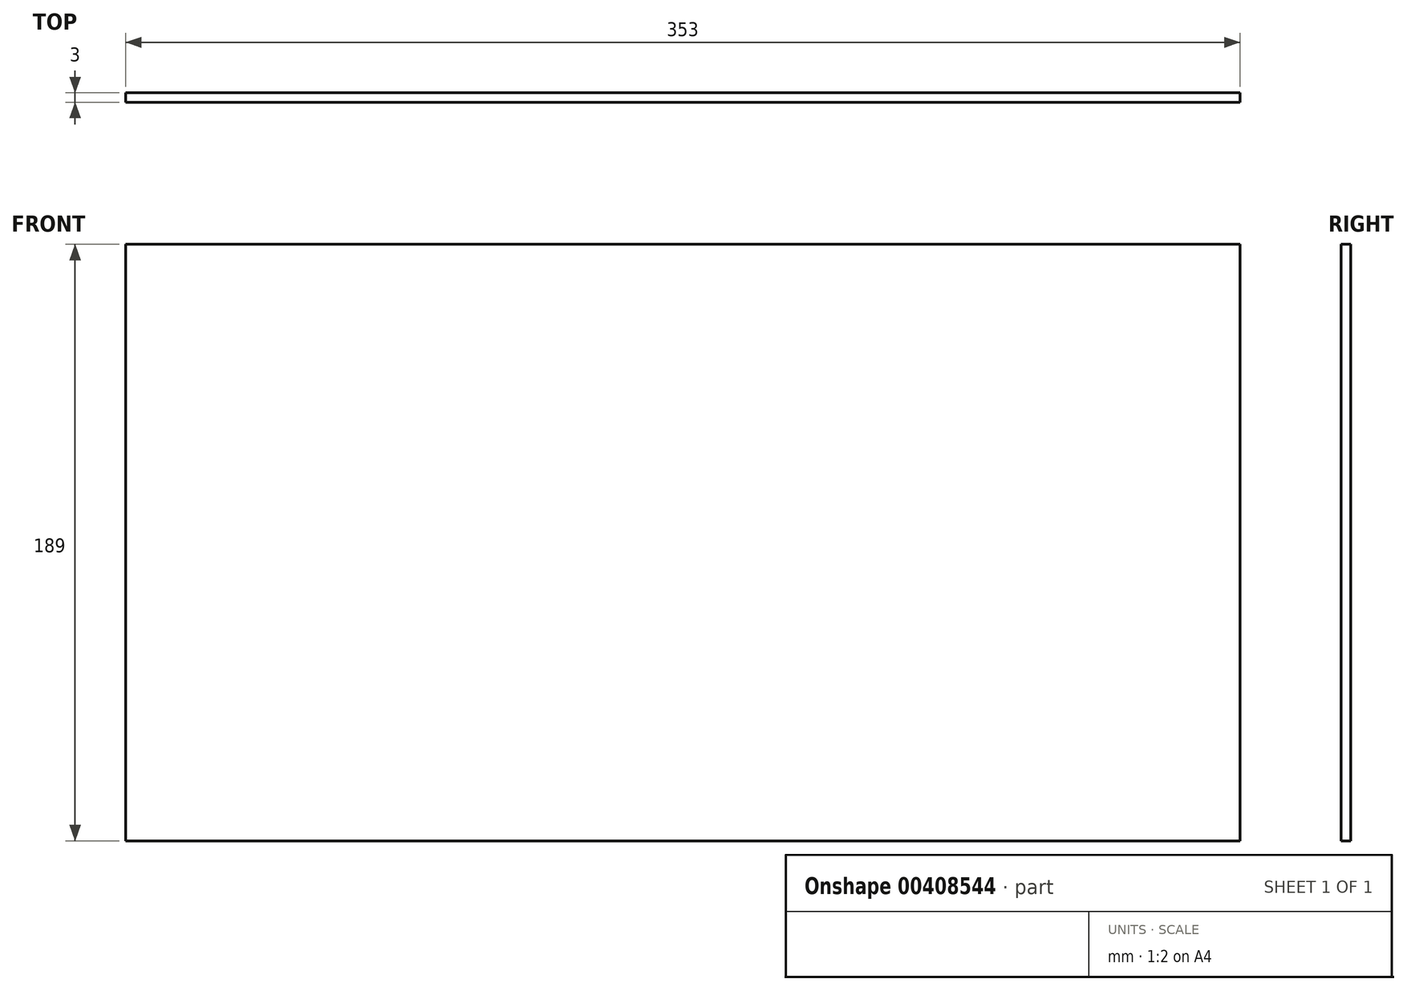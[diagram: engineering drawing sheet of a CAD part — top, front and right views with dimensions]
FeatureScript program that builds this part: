
annotation { "Feature Type Name" : "Feature", "Feature Type Description" : "" }
export const myFeature = defineFeature(function(context is Context, id is Id, definition is map)
    precondition{}
    {
        {
            var Q0;
            Q0=qCreatedBy(makeId("Front.planeOp"),FACE);
            var sketch = newSketch(context, id + "F0", { "sketchPlane" : qUnion([Q0])});
            skLineSegment(sketch, "E0", {"start": v(-194.2, 0) * mm, "end": v(-194.2, 189) * mm});
            skLineSegment(sketch, "E1", {"start": v(-194.2, 189) * mm, "end": v(158.8, 189) * mm});
            skLineSegment(sketch, "E2", {"start": v(158.8, 189) * mm, "end": v(158.8, 0) * mm});
            skLineSegment(sketch, "E3", {"start": v(158.8, 0) * mm, "end": v(-194.2, 0) * mm});
            skSolve(sketch);
        }
        {
            var Q0;
            Q0=makeQuery(id+"F0.imprint","IMPRINT",FACE,{"disambiguationData":[TD([[makeQuery(id+"F0.imprint","IMPRINT",EDGE,{"derivedFrom":sQuery(id+"F0.wireOp",EDGE,"E0")}),-1.0]])]});
            extrude(context, id + "F1", {"entities" : qUnion([Q0]), "depth" : 3 * mm});
        }
    });
